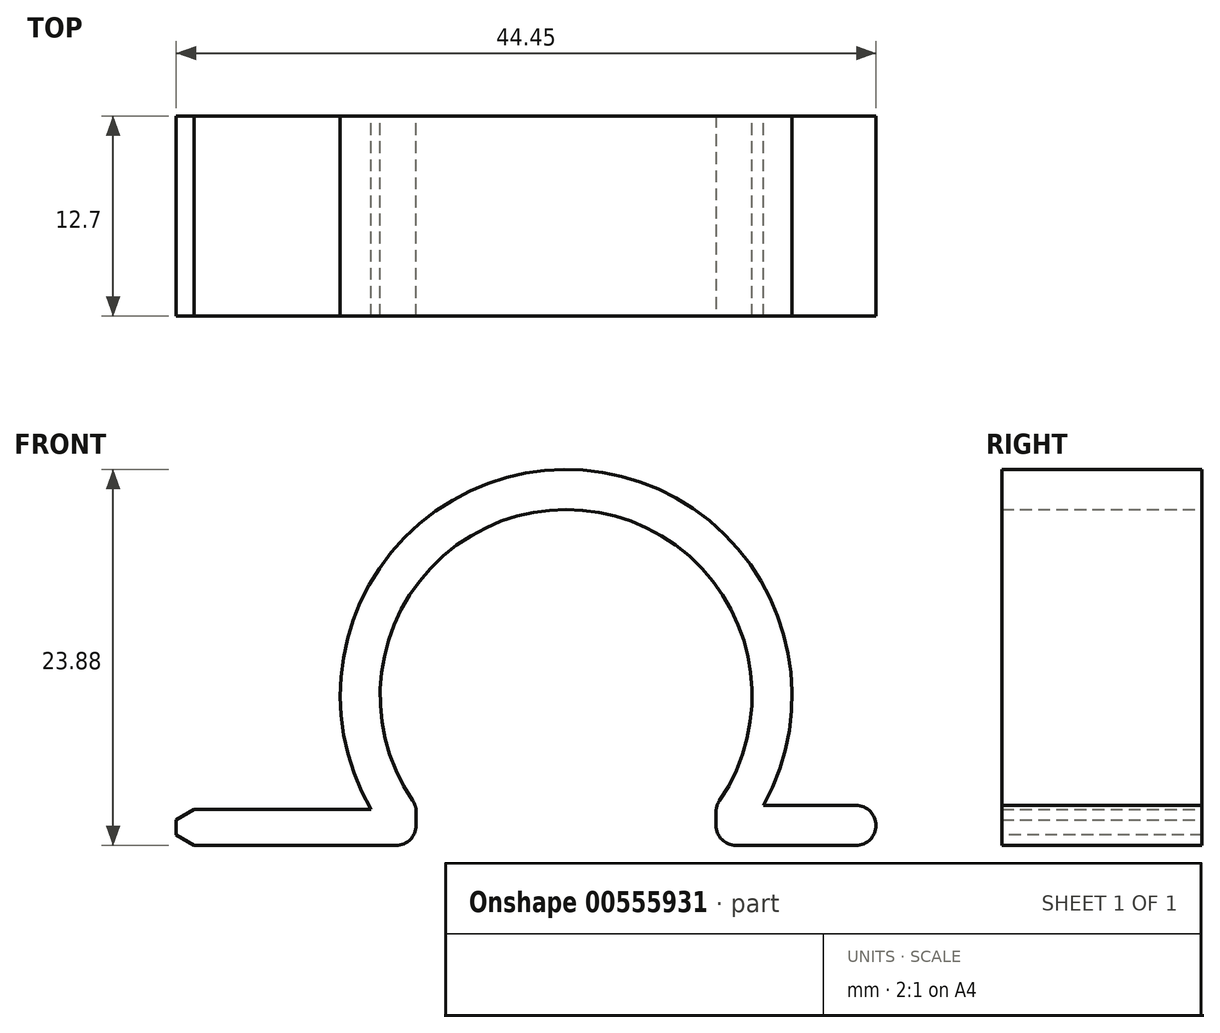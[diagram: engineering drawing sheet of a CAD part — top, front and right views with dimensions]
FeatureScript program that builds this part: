
annotation { "Feature Type Name" : "Feature", "Feature Type Description" : "" }
export const myFeature = defineFeature(function(context is Context, id is Id, definition is map)
    precondition{}
    {
        {
            var Q0;
            Q0=qCreatedBy(makeId("Front.planeOp"),FACE);
            var sketch = newSketch(context, id + "F0", { "sketchPlane" : qUnion([Q0])});
            skLineSegment(sketch, "E0", {"start": v(0, 0) * mm, "end": v(15.24, 0) * mm});
            skLineSegment(sketch, "E1", {"start": v(15.24, 0) * mm, "end": v(15.24, 2.54) * mm});
            skLineSegment(sketch, "E2", {"start": v(15.24, 0) * mm, "end": v(24.77, 0) * mm, "construction": true});
            skLineSegment(sketch, "E3", {"start": v(24.77, 0) * mm, "end": v(24.77, 9.53) * mm, "construction": true});
            skArc(sketch, "E4", {"start": v(34.3, 2.54) * mm, "mid": v(24.77, 21.34) * mm, "end": v(15.24, 2.54) * mm});
            skLineSegment(sketch, "E5", {"start": v(15.24, 2.54) * mm, "end": v(34.3, 2.54) * mm, "construction": true});
            skLineSegment(sketch, "E6", {"start": v(34.3, 2.54) * mm, "end": v(34.3, 0) * mm});
            skLineSegment(sketch, "E7", {"start": v(34.3, 0) * mm, "end": v(44.45, 0) * mm});
            skLineSegment(sketch, "E8.0", {"start": v(37.3, 2.54) * mm, "end": v(44.45, 2.54) * mm});
            skLineSegment(sketch, "E9", {"start": v(44.45, 0) * mm, "end": v(44.45, 2.54) * mm});
            skLineSegment(sketch, "E10", {"start": v(0, 0) * mm, "end": v(0, 2.29) * mm});
            skLineSegment(sketch, "E11", {"start": v(0, 2.29) * mm, "end": v(12.37, 2.29) * mm});
            skArc(sketch, "E12", {"start": v(37.3, 2.54) * mm, "mid": v(24.62, 23.88) * mm, "end": v(12.37, 2.29) * mm});
            skSolve(sketch);
        }
        {
            var Q0;
            Q0=makeQuery(id+"F0.imprint","IMPRINT",FACE,{"disambiguationData":[TD([[makeQuery(id+"F0.imprint","IMPRINT",EDGE,{"derivedFrom":sQuery(id+"F0.wireOp",EDGE,"E0")}),1.0]])]});
            extrude(context, id + "F1", {"entities" : qUnion([Q0]), "depth" : 12.7 * mm, "offsetDistance" : 25.4 * mm});
        }
        {
            var Q0;
            Q0=makeQuery(id+"F1.opExtrude","SWEPT_EDGE",EDGE,{"disambiguationData":[OSD([sQuery(id+"F0.wireOp",EDGE,"E0"),sQuery(id+"F0.wireOp",EDGE,"E10")])]});
            var Q1;
            Q1=makeQuery(id+"F1.opExtrude","SWEPT_EDGE",EDGE,{"disambiguationData":[OSD([sQuery(id+"F0.wireOp",EDGE,"E10"),sQuery(id+"F0.wireOp",EDGE,"E11")])]});
            chamfer(context, id + "F2", {"entities" : qUnion([Q0, Q1]), "chamferType" : ChamferType.OFFSET_ANGLE, "width" : 1.14 * mm, "oppositeDirection" : false, "angle" : 30 * degree, "tangentPropagation" : true});
        }
        {
            var Q0;
            Q0=makeQuery(id+"F1.opExtrude","SWEPT_EDGE",EDGE,{"disambiguationData":[OSD([sQuery(id+"F0.wireOp",EDGE,"E8.0"),sQuery(id+"F0.wireOp",EDGE,"E9")])]});
            var Q1;
            Q1=makeQuery(id+"F1.opExtrude","SWEPT_EDGE",EDGE,{"disambiguationData":[OSD([sQuery(id+"F0.wireOp",EDGE,"E7"),sQuery(id+"F0.wireOp",EDGE,"E9")])]});
            var Q2;
            Q2=makeQuery(id+"F1.opExtrude","SWEPT_EDGE",EDGE,{"disambiguationData":[OSD([sQuery(id+"F0.wireOp",EDGE,"E6"),sQuery(id+"F0.wireOp",EDGE,"E7")])]});
            var Q3;
            Q3=makeQuery(id+"F1.opExtrude","SWEPT_EDGE",EDGE,{"disambiguationData":[OSD([sQuery(id+"F0.wireOp",EDGE,"E4"),sQuery(id+"F0.wireOp",EDGE,"E6")])]});
            var Q4;
            Q4=makeQuery(id+"F1.opExtrude","SWEPT_EDGE",EDGE,{"disambiguationData":[OSD([sQuery(id+"F0.wireOp",EDGE,"E1"),sQuery(id+"F0.wireOp",EDGE,"E4")])]});
            var Q5;
            Q5=makeQuery(id+"F1.opExtrude","SWEPT_EDGE",EDGE,{"disambiguationData":[OSD([sQuery(id+"F0.wireOp",EDGE,"E0"),sQuery(id+"F0.wireOp",EDGE,"E1")])]});
            fillet(context, id + "F3", {"entities" : qUnion([Q0, Q1, Q2, Q3, Q4, Q5]), "radius" : 1.27 * mm, "tangentPropagation" : true, "allowEdgeOverflow" : false});
        }
    });
